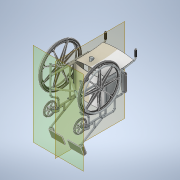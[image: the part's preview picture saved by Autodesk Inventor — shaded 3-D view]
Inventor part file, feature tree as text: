
AUTODESK INVENTOR PART (.ipt)
format: ipt  version: 2021 (Build 250183000, 183)  size: 1,308,672 bytes
history: native  units: mm
features: other x27, plane x3, sketch x1, extrude x1
ambient origin geometry x8: Origin, YZ Plane, XZ Plane, XY Plane, X Axis, Y Axis, Z Axis, Center Point
bodies: Solid1 (feature_tree), Solid2 (feature_tree), Solid3 (feature_tree), Solid4 (feature_tree), Solid5 (feature_tree), Solid6 (feature_tree), Solid7 (feature_tree), Solid8 (feature_tree), Solid9 (feature_tree), Solid10 (feature_tree), Solid11 (feature_tree), Solid12 (feature_tree), Solid13 (feature_tree), Solid14 (feature_tree), Solid15 (feature_tree), Solid16 (feature_tree), Solid17 (feature_tree), Solid18 (feature_tree), Solid19 (feature_tree), Solid20 (feature_tree), Solid21 (feature_tree), Solid22 (feature_tree), Solid23 (feature_tree), Solid24 (feature_tree), Solid25 (feature_tree), Solid26 (feature_tree), Solid27 (feature_tree)
feature tree (32):
  plane  "Work Plane1"
  plane  "Work Plane2"
  sketch  "Sketch1"  dims[d0=215.0mm d1=-440.0mm d9=-890.0mm d17=30.0mm d18=0.0mm d20=50.0mm d25=10.0mm d26=12.217305mm d27=23.911011mm d28=30.0mm d29=30.0mm]
  plane  "Work Plane4"
  extrude  "Extrusion3"  [1 undecoded]
  other  "SideFrame_1:1"
  other  "SideFrame_1:2"
  other  "SideFrame_1:3"
  other  "SideFrame_1:4"
  other  "SideFrame_1:5"
  other  "SideFrame_1:6"
  other  "SideFrame_1:7"
  other  "Arm_2:1"
  other  "Arm_2:2"
  other  "Arm_3:1"
  other  "Arm_3:2"
  other  "ArmPad_4:1"
  other  "ArmPad_5:1"
  other  "Seat_6:1"
  other  "WheelLarge_7:1"
  other  "WheelLarge_7:2"
  other  "WheelLarge_8:1"
  other  "WheelLarge_8:2"
  other  "WheelSmall_16:1"
  other  "CasterFork_17:1"
  other  "WheelSmall_16:2"
  other  "CasterFork_17:2"
  other  "Back_11:1"
  other  "FootRest_12:1"
  other  "FootRest_13:1"
  other  "Grip_14:1"
  other  "Grip_15:1"
note: 1 required parameter value undecoded (feature->parameter linkage not recoverable at this tier; creation-order binding heuristic only, values carry confidence <= 0.55)
